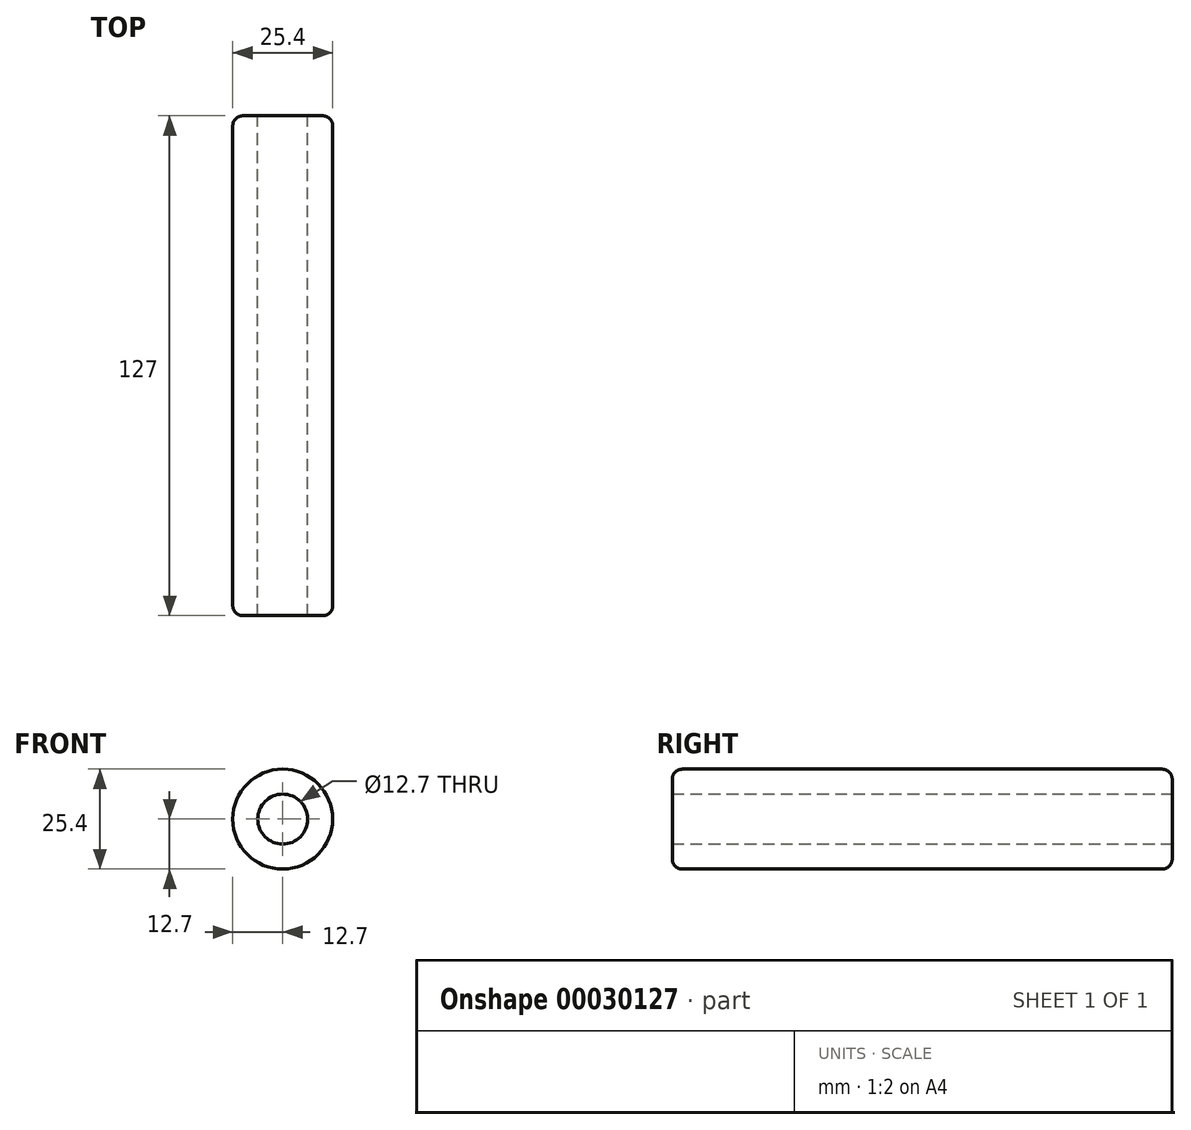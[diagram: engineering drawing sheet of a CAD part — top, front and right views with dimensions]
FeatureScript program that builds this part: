
annotation { "Feature Type Name" : "Feature", "Feature Type Description" : "" }
export const myFeature = defineFeature(function(context is Context, id is Id, definition is map)
    precondition{}
    {
        {
            var Q0;
            Q0=qCreatedBy(makeId("Front.planeOp"),FACE);
            var sketch = newSketch(context, id + "F0", { "sketchPlane" : qUnion([Q0])});
            skCircle(sketch, "E0", {"center": v(0, 0) * mm, "radius": 12.7 * mm});
            skSolve(sketch);
        }
        {
            var Q0;
            Q0 = qSketchRegion(id + "F0", true);
            extrude(context, id + "F1", {"entities" : qUnion([Q0]), "endBound" : BoundingType.SYMMETRIC, "depth" : 127 * mm});
        }
        {
            var Q0;
            Q0=makeQuery(id+"F1.opExtrude","CAP_FACE",FACE,{"disambiguationData":[OSD([sQuery(id+"F0.wireOp",EDGE,"E0")])],"isStart":true});
            var sketch = newSketch(context, id + "F2", { "sketchPlane" : qUnion([Q0])});
            skPoint(sketch, "E1", {"position": v(0, 0) * mm});
            skSolve(sketch);
        }
        {
            var Q0;
            Q0=sQuery(id+"F2.wireOp",VERTEX,"E1");
            var Q1;
            Q1=makeQuery(id+"F1.opExtrude","SWEPT_BODY",BODY,{"disambiguationData":[OSD([sQuery(id+"F0.wireOp",EDGE,"E0")])]});
            hole(context, id + "F3", {"style" : HoleStyle.SIMPLE, "holeDiameter" : 12.7 * mm, "endStyle" : HoleEndStyle.THROUGH, "locations" : qUnion([Q0]), "scope" : qUnion([Q1])});
        }
        {
            var Q0;
            Q0=makeQuery(id+"F1.opExtrude","CAP_EDGE",EDGE,{"disambiguationData":[OSD([sQuery(id+"F0.wireOp",EDGE,"E0")])],"isStart":false});
            var Q1;
            Q1=makeQuery(id+"F3.hole-0.boolean.opBoolean","INTERSECT",EDGE,{"derivedFrom":[makeQuery(id+"F1.opExtrude","CAP_FACE",FACE,{"disambiguationData":[OSD([sQuery(id+"F0.wireOp",EDGE,"E0")])],"isStart":false}),makeQuery(id+"F3.hole-0.opRevolve","SWEPT_FACE",FACE,{"disambiguationData":[OSD([sQuery(id+"F3.hole-0.sketch.wireOp",EDGE,"core_line_2")])]})]});
            var Q2;
            Q2=makeQuery(id+"F3.hole-0.boolean.opBoolean","COPY",EDGE,{"derivedFrom":makeQuery(id+"F3.hole-0.opRevolve","SWEPT_EDGE",EDGE,{"disambiguationData":[OSD([sQuery(id+"F3.hole-0.sketch.wireOp",EDGE,"core_line_2"),sQuery(id+"F3.hole-0.sketch.wireOp",EDGE,"core_line_3")])]})});
            var Q3;
            Q3=makeQuery(id+"F1.opExtrude","CAP_EDGE",EDGE,{"disambiguationData":[OSD([sQuery(id+"F0.wireOp",EDGE,"E0")])],"isStart":true});
            fillet(context, id + "F4", {"entities" : qUnion([Q0, Q1, Q2, Q3]), "radius" : 2.54 * mm, "tangentPropagation" : true, "allowEdgeOverflow" : false});
        }
    });
